AUTODESK INVENTOR PART (.ipt)
format: ipt  version: 2023 (Build 270158000, 158)  size: 162,816 bytes
history: native  units: mm
features: extrude x3, sketch x3, projected_geometry x1
ambient origin geometry x8: Origin, YZ Plane, XZ Plane, XY Plane, X Axis, Y Axis, Z Axis, Center Point
bodies: Solid1 (feature_tree)
feature tree (7):
  extrude  "Extrusion1"  Depth=142.0mm
  extrude  "Extrusion2"  Depth=120.0mm
  extrude  "Extrusion3"  Depth=5.0mm
  sketch  "Sketch1"  dims[d0=30.0mm d1=142.0mm]
  sketch  "Sketch2"  dims[d2=10.0mm d3=0.0mm d4=120.0mm]
  sketch  "Sketch3"  dims[d5=5.0mm d6=0.0mm d7=105.0mm d8=7.112mm d9=5.0mm d10=0.0mm]
  projected_geometry  "Projected Loop1"
